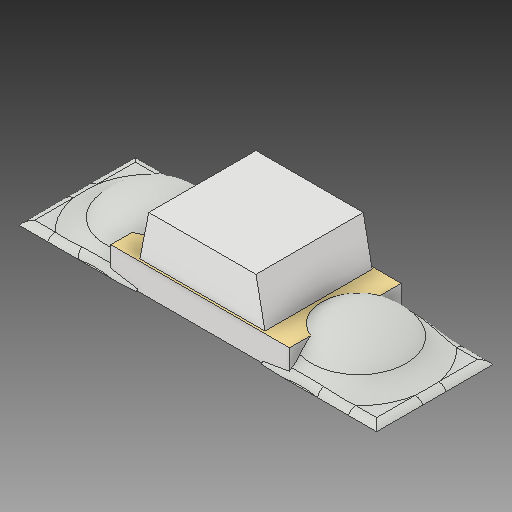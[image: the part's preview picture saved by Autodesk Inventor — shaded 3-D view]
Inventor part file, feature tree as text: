
AUTODESK INVENTOR PART (.ipt)
format: ipt  version: 2019.4 (Build 234330000, 330)  size: 218,112 bytes
history: native  units: mm
features: mirror x1, other x1
ambient origin geometry x8: Origin, YZ Plane, XZ Plane, XY Plane, X Axis, Y Axis, Z Axis, Center Point
bodies: Solid1 (feature_tree), Solid2 (feature_tree)
feature tree (2):
  mirror  "Mirror3"
  other  "Boss-Extrude5"
